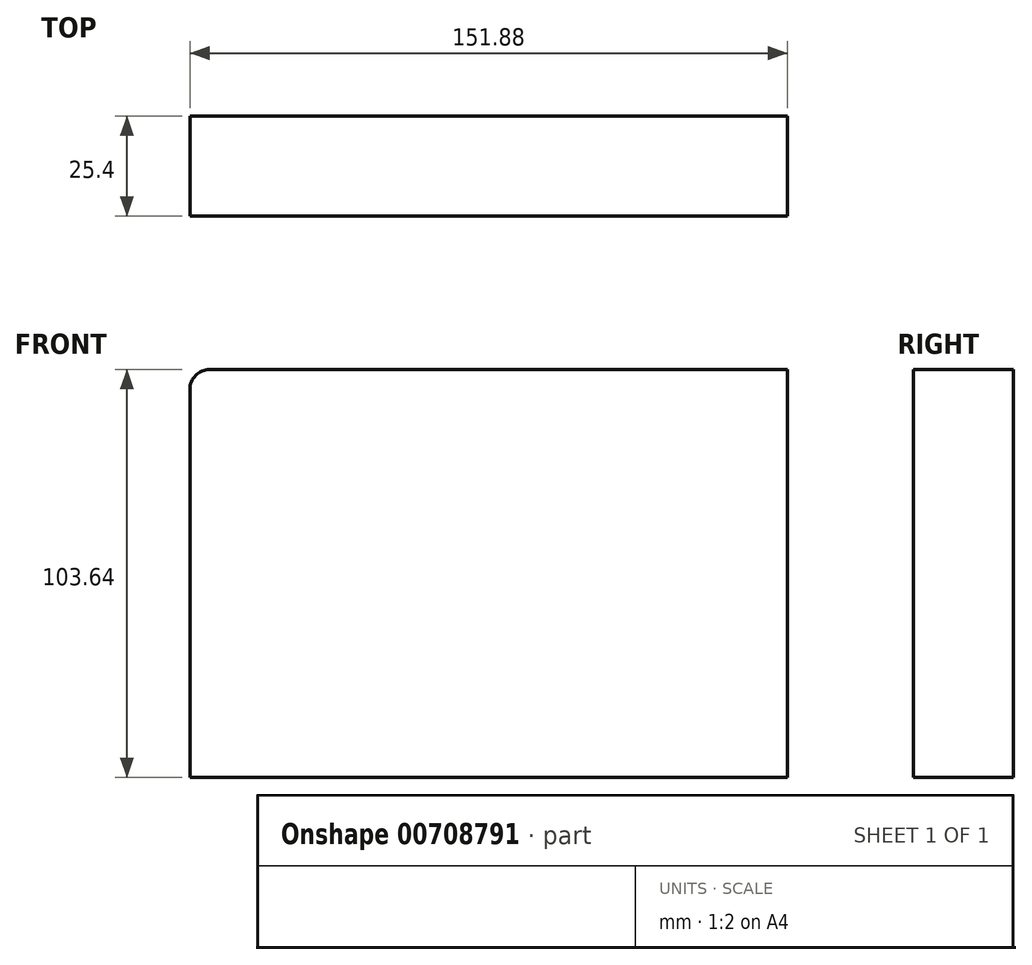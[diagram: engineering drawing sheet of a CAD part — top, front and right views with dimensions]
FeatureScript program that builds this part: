
annotation { "Feature Type Name" : "Feature", "Feature Type Description" : "" }
export const myFeature = defineFeature(function(context is Context, id is Id, definition is map)
    precondition{}
    {
        {
            var Q0;
            Q0=qCreatedBy(makeId("Front.planeOp"),FACE);
            var sketch = newSketch(context, id + "F0", { "sketchPlane" : qUnion([Q0])});
            skLineSegment(sketch, "E0.bottom", {"start": v(-98.66, -66.55) * mm, "end": v(53.22, -66.55) * mm});
            skLineSegment(sketch, "E0.top", {"start": v(-98.66, 37.09) * mm, "end": v(53.22, 37.09) * mm});
            skLineSegment(sketch, "E0.left", {"start": v(-98.66, -66.55) * mm, "end": v(-98.66, 37.09) * mm});
            skLineSegment(sketch, "E0.right", {"start": v(53.22, -66.55) * mm, "end": v(53.22, 37.09) * mm});
            skSolve(sketch);
        }
        {
            var Q0;
            Q0 = qSketchRegion(id + "F0", true);
            extrude(context, id + "F1", {"entities" : qUnion([Q0]), "depth" : 25.4 * mm, "offsetDistance" : 25.4 * mm});
        }
        {
            var Q0;
            Q0=makeQuery(id+"F1.opExtrude","SWEPT_EDGE",EDGE,{"disambiguationData":[OSD([sQuery(id+"F0.wireOp",EDGE,"E0.top"),sQuery(id+"F0.wireOp",EDGE,"E0.left")])]});
            fillet(context, id + "F2", {"entities" : qUnion([Q0]), "radius" : 5.08 * mm, "tangentPropagation" : true, "allowEdgeOverflow" : false});
        }
    });
